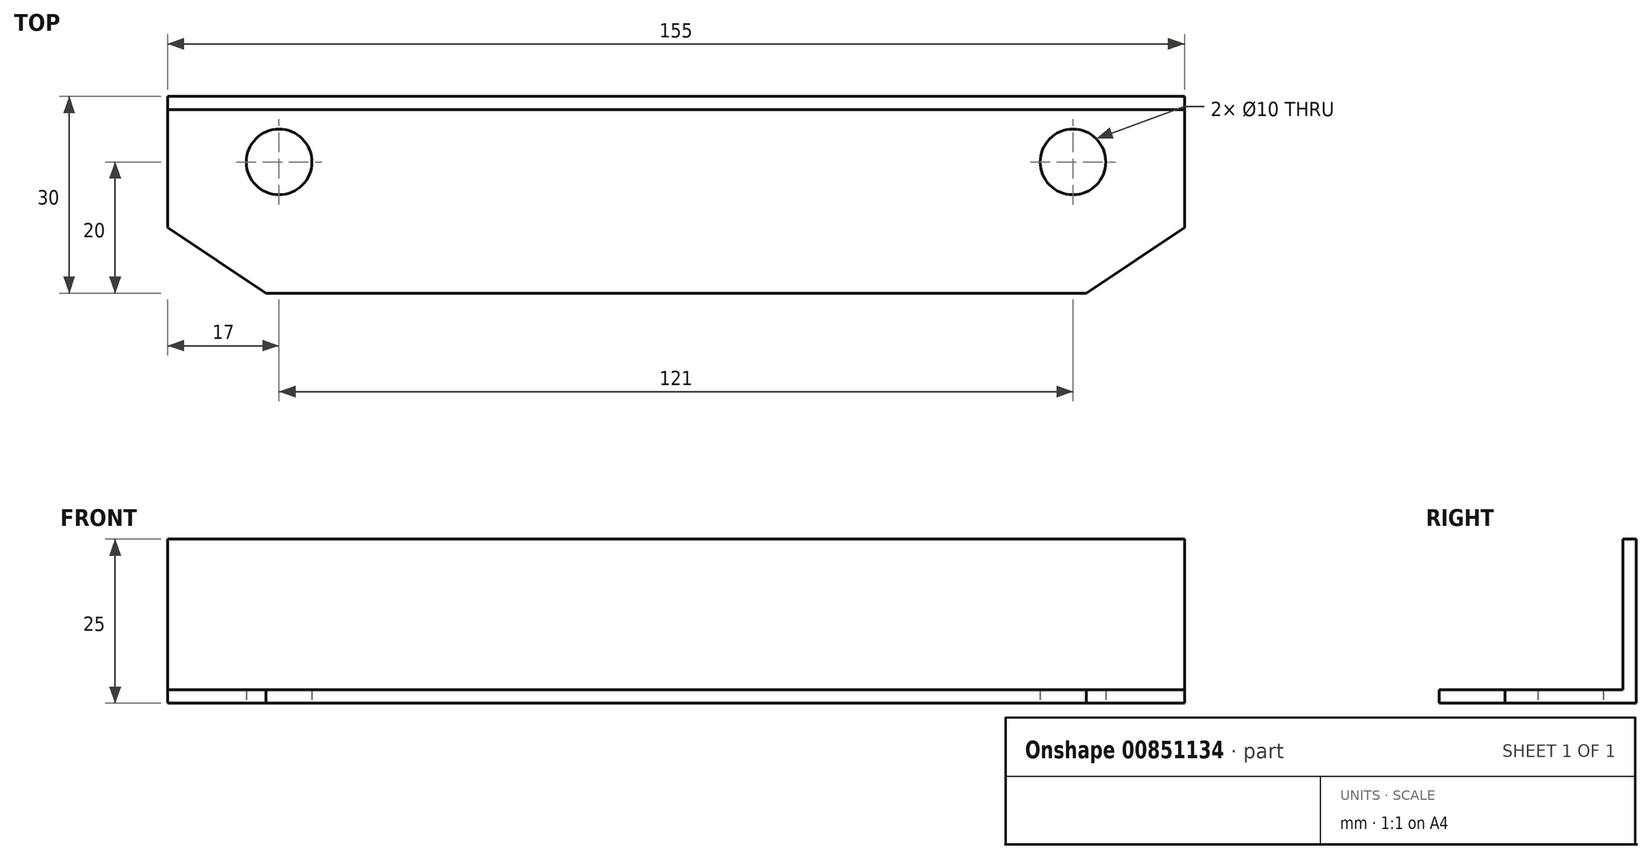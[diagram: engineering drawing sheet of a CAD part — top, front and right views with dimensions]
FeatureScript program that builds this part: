
annotation { "Feature Type Name" : "Feature", "Feature Type Description" : "" }
export const myFeature = defineFeature(function(context is Context, id is Id, definition is map)
    precondition{}
    {
        {
            var Q0;
            Q0=qCreatedBy(makeId("Top.planeOp"),FACE);
            var sketch = newSketch(context, id + "F0", { "sketchPlane" : qUnion([Q0])});
            skLineSegment(sketch, "E0.top", {"start": v(-62.5, -30) * mm, "end": v(62.5, -30) * mm});
            skPoint(sketch, "E0.middle", {"position": v(0, 0) * mm});
            skLineSegment(sketch, "E1", {"start": v(-77.5, -20) * mm, "end": v(-62.5, -30) * mm});
            skPoint(sketch, "E2.orphan", {"position": v(-77.5, -30) * mm});
            skLineSegment(sketch, "E3", {"start": v(0, 41.12) * mm, "end": v(0, -35.6) * mm, "construction": true});
            skLineSegment(sketch, "E4.MirrorCS", {"start": v(77.5, -20) * mm, "end": v(62.5, -30) * mm});
            skPoint(sketch, "E5.orphan", {"position": v(77.5, -30) * mm});
            skLineSegment(sketch, "E6", {"start": v(-77.5, 0) * mm, "end": v(77.5, 0) * mm});
            skLineSegment(sketch, "E7", {"start": v(-77.5, 0) * mm, "end": v(-77.5, -20) * mm});
            skLineSegment(sketch, "E8.MirrorCS", {"start": v(77.5, 0) * mm, "end": v(77.5, -20) * mm});
            skCircle(sketch, "E9", {"center": v(-60.5, -10) * mm, "radius": 5 * mm});
            skCircle(sketch, "E10.MirrorC", {"center": v(60.5, -10) * mm, "radius": 5 * mm});
            skLineSegment(sketch, "E11.top", {"start": v(-77.5, -2) * mm, "end": v(77.5, -2) * mm});
            skLineSegment(sketch, "E11.left", {"start": v(-77.5, 0) * mm, "end": v(-77.5, -2) * mm});
            skLineSegment(sketch, "E11.right", {"start": v(77.5, 0) * mm, "end": v(77.5, -2) * mm});
            skSolve(sketch);
        }
        {
            var Q0;
            Q0=makeQuery(id+"F0.imprint","IMPRINT",FACE,{"disambiguationData":[TD([[makeQuery(id+"F0.imprint","IMPRINT",EDGE,{"derivedFrom":sQuery(id+"F0.wireOp",EDGE,"E0.top")}),1.0]])]});
            var Q1;
            Q1=makeQuery(id+"F0.imprint","IMPRINT",FACE,{"disambiguationData":[TD([[makeQuery(id+"F0.imprint","IMPRINT",EDGE,{"derivedFrom":sQuery(id+"F0.wireOp",EDGE,"E6")}),-1.0]])]});
            extrude(context, id + "F1", {"entities" : qUnion([Q0, Q1]), "depth" : 2 * mm, "offsetDistance" : 25 * mm});
        }
        {
            var Q0;
            Q0=makeQuery(id+"F0.imprint","IMPRINT",FACE,{"disambiguationData":[TD([[makeQuery(id+"F0.imprint","IMPRINT",EDGE,{"derivedFrom":sQuery(id+"F0.wireOp",EDGE,"E6")}),-1.0]])]});
            extrude(context, id + "F2", {"entities" : qUnion([Q0]), "operationType" : NewBodyOperationType.ADD, "depth" : 25 * mm, "offsetDistance" : 25 * mm});
        }
    });
